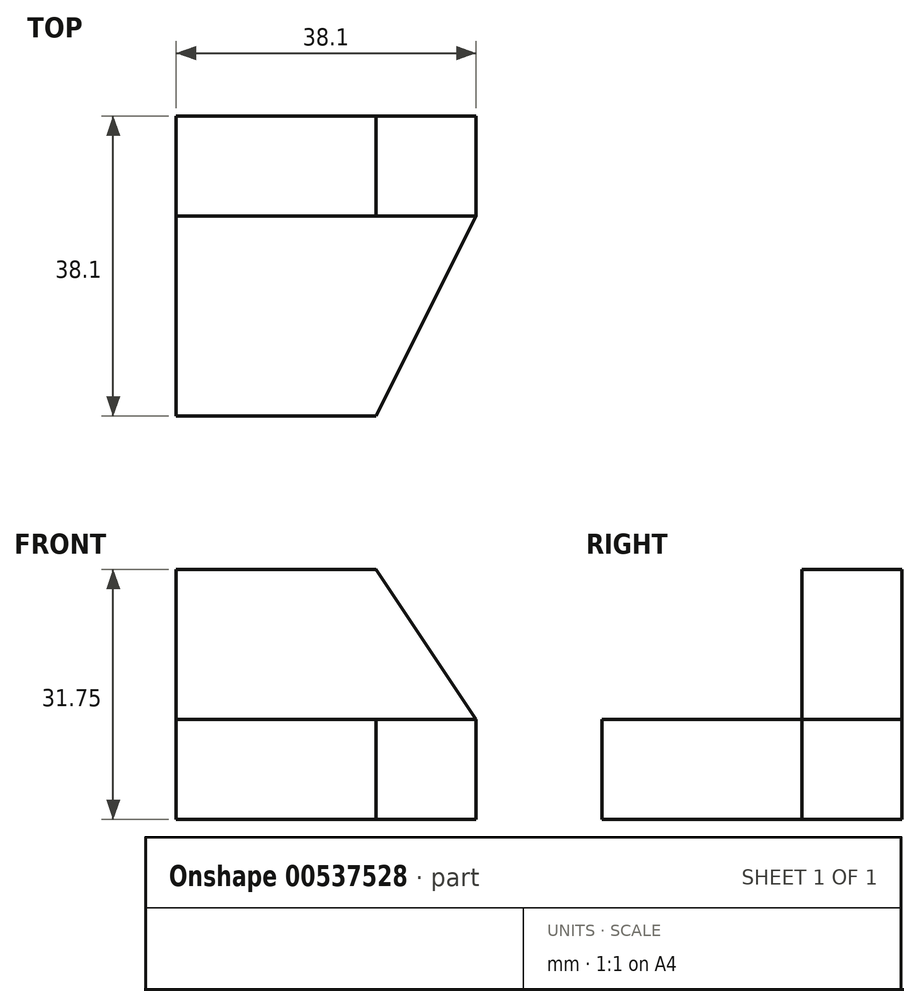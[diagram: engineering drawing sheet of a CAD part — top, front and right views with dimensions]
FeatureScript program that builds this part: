
annotation { "Feature Type Name" : "Feature", "Feature Type Description" : "" }
export const myFeature = defineFeature(function(context is Context, id is Id, definition is map)
    precondition{}
    {
        {
            var Q0;
            Q0=qCreatedBy(makeId("Right.planeOp"),FACE);
            var sketch = newSketch(context, id + "F0", { "sketchPlane" : qUnion([Q0])});
            skLineSegment(sketch, "E0", {"start": v(0, 0) * mm, "end": v(38.1, 0) * mm});
            skLineSegment(sketch, "E1", {"start": v(38.1, 0) * mm, "end": v(38.1, 31.75) * mm});
            skLineSegment(sketch, "E2", {"start": v(38.1, 31.75) * mm, "end": v(25.4, 31.75) * mm});
            skLineSegment(sketch, "E3", {"start": v(25.4, 31.75) * mm, "end": v(25.4, 12.7) * mm});
            skLineSegment(sketch, "E4", {"start": v(25.4, 12.7) * mm, "end": v(0, 12.7) * mm});
            skLineSegment(sketch, "E5", {"start": v(0, 12.7) * mm, "end": v(0, 0) * mm});
            skSolve(sketch);
        }
        {
            var Q0;
            Q0=makeQuery(id+"F0.imprint","IMPRINT",FACE,{"disambiguationData":[TD([[makeQuery(id+"F0.imprint","IMPRINT",EDGE,{"derivedFrom":sQuery(id+"F0.wireOp",EDGE,"E0")}),1.0]])]});
            extrude(context, id + "F1", {"entities" : qUnion([Q0]), "oppositeDirection" : true, "depth" : 38.1 * mm, "offsetDistance" : 25.4 * mm});
        }
        {
            var Q0;
            Q0=makeQuery(id+"F1.opExtrude","SWEPT_FACE",FACE,{"disambiguationData":[OSD([sQuery(id+"F0.wireOp",EDGE,"E3")])]});
            var sketch = newSketch(context, id + "F2", { "sketchPlane" : qUnion([Q0])});
            skLineSegment(sketch, "E6", {"start": v(-12.7, 31.75) * mm, "end": v(0, 12.7) * mm});
            skSolve(sketch);
        }
        {
            var Q0;
            Q0=makeQuery(id+"F1.opExtrude","SWEPT_FACE",FACE,{"disambiguationData":[OSD([sQuery(id+"F0.wireOp",EDGE,"E4")])]});
            var sketch = newSketch(context, id + "F3", { "sketchPlane" : qUnion([Q0])});
            skLineSegment(sketch, "E7", {"start": v(-12.7, 0) * mm, "end": v(0, 25.4) * mm});
            skSolve(sketch);
        }
        {
            var Q0;
            {var subQ0=sQuery(id+"F2.wireOp",EDGE,"E6");Q0=makeQuery(id+"F2.imprint","IMPRINT",FACE,{"disambiguationData":[TD([[makeQuery(id+"F2.imprint","IMPRINT",EDGE,{"derivedFrom":subQ0}),1.0]])]});}
            extrude(context, id + "F4", {"entities" : qUnion([Q0]), "operationType" : NewBodyOperationType.REMOVE, "oppositeDirection" : true, "depth" : 25.4 * mm, "offsetDistance" : 25.4 * mm});
        }
        {
            var Q0;
            {var subQ0=sQuery(id+"F3.wireOp",EDGE,"E7");Q0=makeQuery(id+"F3.imprint","IMPRINT",FACE,{"disambiguationData":[TD([[makeQuery(id+"F3.imprint","IMPRINT",EDGE,{"derivedFrom":subQ0}),-1.0]])]});}
            extrude(context, id + "F5", {"entities" : qUnion([Q0]), "operationType" : NewBodyOperationType.REMOVE, "oppositeDirection" : true, "depth" : 25.4 * mm, "offsetDistance" : 25.4 * mm});
        }
    });
